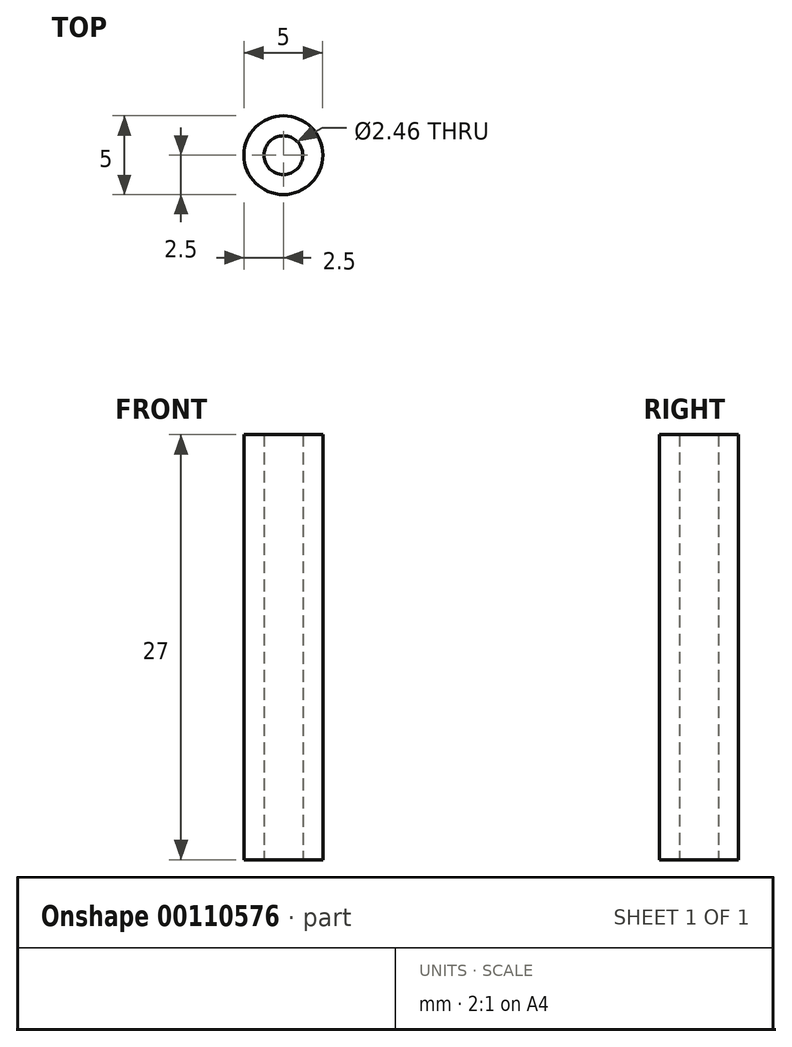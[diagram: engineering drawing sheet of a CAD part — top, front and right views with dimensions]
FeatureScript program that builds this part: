
annotation { "Feature Type Name" : "Feature", "Feature Type Description" : "" }
export const myFeature = defineFeature(function(context is Context, id is Id, definition is map)
    precondition{}
    {
        {
            var Q0;
            Q0=qCreatedBy(makeId("Top.planeOp"),FACE);
            var sketch = newSketch(context, id + "F0", { "sketchPlane" : qUnion([Q0])});
            skCircle(sketch, "E0", {"center": v(0, 0) * mm, "radius": 2.5 * mm});
            skCircle(sketch, "E1", {"center": v(0, 0) * mm, "radius": 1.23 * mm});
            skSolve(sketch);
        }
        {
            var Q0;
            Q0=makeQuery(id+"F0.imprint","IMPRINT",FACE,{"disambiguationData":[TD([[makeQuery(id+"F0.imprint","IMPRINT",EDGE,{"derivedFrom":sQuery(id+"F0.wireOp",EDGE,"E0")}),1.0]])]});
            extrude(context, id + "F1", {"entities" : qUnion([Q0]), "depth" : 27 * mm});
        }
    });
